# Revit family: Izveshchatel pozharnyy ruchnoy IPR 535-Ekhd-A «MOROZ»
name_source: partatom
category: Пожарная сигнализация
units: mm (PartAtom-declared; Revit-internal decimal feet)

## family parameters
Всегда вертикально = Да
Заголовок OmniClass = Communication and Data Processing Equipment
На основе рабочей плоскости = Нет
Номер OmniClass = 23.85.50.17
Общий = Нет
При загрузке вырезать с полостями = Нет
Размер круглого соединителя = Использовать диаметр
Сохранять ориентацию аннотаций = Нет
Тип детали = Нормальный
Точка принадлежности помещению = Нет

## types (2) — shared parameters
ADSK_Единица измерения = шт.
ADSK_Завод-изготовитель = ООО НПП «МАГНИТО-КОНТАКТ»
ADSK_Материал = Алюминиевый сплав
ADSK_Наименование = Извещатель пожарный ручной ИПР 535-Ехd-А «МОРОЗ» 1EX DB IIC T6…T5 DB / EX TB IIIC T85°C…T100°C DB / EX IA IIIC T85°C…T100°C DA
ADSK_Обозначение = АТФЕ.425211.001ПС
ADSK_Примечание = Извещатели пожарные ручные ИПР 535-Ехd-А «МОРОЗ» должны применяться с кабельными вводами МКВ или Ех МКВМ (см. таблицу) и Ех-заглушками завода-изготовителя или другими кабельными вводами и заглушками, соответствующими требованиям ТР ТС 012/2011, имеющими действующий сертификат соответствия, обеспечивающими вид и уровень взрывозащиты, а так же степень защиты оболочки, соответствующие ИПР 535-Ехd-А «МОРОЗ». Материал уплотнительных колец должен быть рассчитан на работу при температуре окружающей среды, соответствующей условиям эксплуатации извещателя.
ADSK_Размер_Высота = 110 мм
ADSK_Размер_Диаметр = 6 мм
ADSK_Размер_Длина = 210 мм
URL = https://m-kontakt.ru
Диапазон рабочих температур = -60°С ... + 70°С (Т6); -60°С ... + 95°С (Т5)
Заглушка = Да
Звено цепочки = Да
Изготовитель = ООО НПП «МАГНИТО-КОНТАКТ»
Искробезопасные параметры = Ui - 30 B,Ii - 100 мA,Pi - 1 Вт,Li - 10 мкГн,Ci - 50 пФ
Кабельный ввод = Да
Класс по степени защиты = III по ГОСТ 12.2.007.0
Левый кабельный ввод = Да
Максимально допустимая влажность = 98%
Наклейка = Наклейка
Напряжение питания = 9 - 30 В
Описание = Извещатель пожарный ручной ИПР 535-Ехd-А «МОРОЗ» (в дальнейшем извещатель) предназначен для ручного включения сигнала тревоги на приемно-контрольном приборе (далее ПКП), в помещениях зданий и сооружений различного назначения.Извещатель приводится в действие удалением чеки-застежки. Не более чем через 4 секунды извещатель перейдет в режим тревоги с постоянным свечением красного индикаторного светодиода и передаст сигнал тревоги на ПКП. Возврат извещателя в исходное состояние (дежурный режим) осуществляется установкой чеки-застежки на штатное место с помощью спец. инструмента и сбрасыванием сигнала тревоги на ПКП. Индикация дежурного режима осуществляется промаргиванием светодиода.
Правый кабельный ввод = Да
Светопропуск = Светопропуск
Средний потребляемый ток = не более 50 мкА
Степень зашиты корпуса = IP66/IP67
Ток потребления в режиме "Пожар" = 10±2 мА (при 9 В),
не более 20±2 мА (при 30 В)
zero-valued in all types: Отметка по умолчанию

## per-type parameters (varying)
| type | ADSK_Наименование краткое | Пружинный шплинт |
| ИЗВЕЩАТЕЛЬ ПОЖАРНЫЙ РУЧНОЙ ВЗРЫВОЗАЩИЩЁННЫЙ ИПР 535-ЕХD-А «МОРОЗ» ТИП А | ИПР 535-Ехd-А «МОРОЗ» тип А | Нет |
| ИЗВЕЩАТЕЛЬ ПОЖАРНЫЙ РУЧНОЙ ВЗРЫВОЗАЩИЩЁННЫЙ ИПР 535-ЕХD-А «МОРОЗ» ТИП Б | ИПР 535-Ехd-А «МОРОЗ» тип Б | Да |
